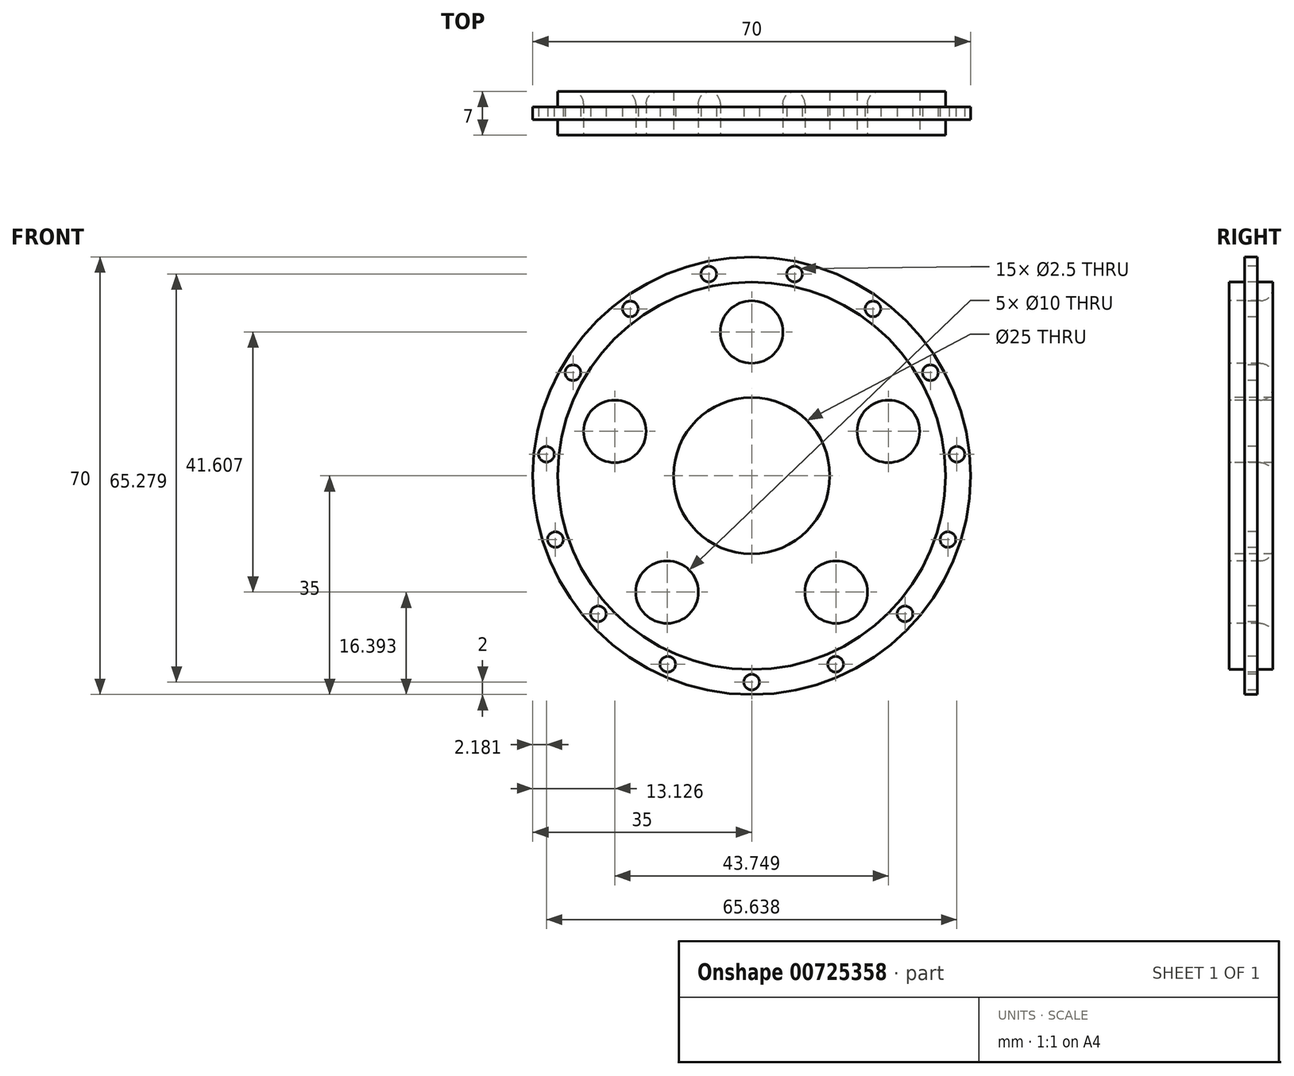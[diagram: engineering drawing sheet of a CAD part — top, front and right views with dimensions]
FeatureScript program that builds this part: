
annotation { "Feature Type Name" : "Feature", "Feature Type Description" : "" }
export const myFeature = defineFeature(function(context is Context, id is Id, definition is map)
    precondition{}
    {
        {
            var Q0;
            Q0=qCreatedBy(makeId("Front.planeOp"),FACE);
            var sketch = newSketch(context, id + "F0", { "sketchPlane" : qUnion([Q0])});
            skCircle(sketch, "E0", {"center": v(0, 0) * mm, "radius": 35 * mm});
            skSolve(sketch);
        }
        {
            var Q0;
            Q0=qSketchRegion(id+"F0",true);
            extrude(context, id + "F1", {"entities" : qUnion([Q0]), "oppositeDirection" : true, "depth" : 3 * mm, "hasSecondDirection" : true, "secondDirectionOppositeDirection" : false, "secondDirectionDepth" : 4 * mm, "offsetDistance" : 25 * mm});
        }
        {
            var Q0;
            Q0=makeQuery(id+"F1.opExtrude","CAP_FACE",FACE,{"disambiguationData":[OSD([sQuery(id+"F0.wireOp",EDGE,"E0")])],"isStart":true});
            var sketch = newSketch(context, id + "F2", { "sketchPlane" : qUnion([Q0])});
            skCircle(sketch, "E1", {"center": v(0, 0) * mm, "radius": 12.5 * mm});
            skSolve(sketch);
        }
        {
            var Q0;
            Q0=qSketchRegion(id+"F2",true);
            extrude(context, id + "F3", {"entities" : qUnion([Q0]), "operationType" : NewBodyOperationType.REMOVE, "oppositeDirection" : true, "depth" : 25 * mm});
        }
        {
            var Q0;
            Q0=makeQuery(id+"F1.opExtrude","CAP_FACE",FACE,{"disambiguationData":[OSD([sQuery(id+"F0.wireOp",EDGE,"E0")])],"isStart":true});
            var sketch = newSketch(context, id + "F4", { "sketchPlane" : qUnion([Q0])});
            skCircle(sketch, "E2", {"center": v(0, 23) * mm, "radius": 5 * mm});
            skLineSegment(sketch, "E3", {"start": v(0, 31) * mm, "end": v(0, 15) * mm, "construction": true});
            skCircle(sketch, "E4.1.0", {"center": v(-21.87, 7.1) * mm, "radius": 5 * mm});
            skCircle(sketch, "E4.2.0", {"center": v(-13.52, -18.6) * mm, "radius": 5 * mm});
            skPoint(sketch, "E4.center", {"position": v(0, 0) * mm});
            skCircle(sketch, "E5", {"center": v(0, 0) * mm, "radius": 15 * mm, "construction": true});
            skCircle(sketch, "E6", {"center": v(0, 0) * mm, "radius": 31 * mm, "construction": true});
            skCircle(sketch, "E7.1.3.0", {"center": v(13.52, -18.6) * mm, "radius": 5 * mm});
            skCircle(sketch, "E8.1.4.0", {"center": v(21.87, 7.1) * mm, "radius": 5 * mm});
            skSolve(sketch);
        }
        {
            var Q0;
            Q0=qSketchRegion(id+"F4",true);
            extrude(context, id + "F5", {"entities" : qUnion([Q0]), "operationType" : NewBodyOperationType.REMOVE, "oppositeDirection" : true, "depth" : 25 * mm});
        }
        {
            var Q0;
            Q0=makeQuery(id+"F1.opExtrude","CAP_FACE",FACE,{"disambiguationData":[OSD([sQuery(id+"F0.wireOp",EDGE,"E0")])],"isStart":true});
            var sketch = newSketch(context, id + "F6", { "sketchPlane" : qUnion([Q0])});
            skCircle(sketch, "E9", {"center": v(0, 0) * mm, "radius": 15 * mm, "construction": true});
            skSolve(sketch);
        }
        {
            var Q0;
            Q0=makeQuery(id+"F5.boolean.opBoolean","COPY",EDGE,{"derivedFrom":makeQuery(id+"F5.opExtrude","CAP_EDGE",EDGE,{"disambiguationData":[OSD([sQuery(id+"F4.wireOp",EDGE,"E2")])],"isStart":true})});
            var Q1;
            Q1=makeQuery(id+"F5.boolean.opBoolean","COPY",EDGE,{"derivedFrom":makeQuery(id+"F5.opExtrude","CAP_EDGE",EDGE,{"disambiguationData":[OSD([sQuery(id+"F4.wireOp",EDGE,"E4.1.0")])],"isStart":true})});
            var Q2;
            Q2=makeQuery(id+"F5.boolean.opBoolean","COPY",EDGE,{"derivedFrom":makeQuery(id+"F5.opExtrude","CAP_EDGE",EDGE,{"disambiguationData":[OSD([sQuery(id+"F4.wireOp",EDGE,"E4.2.0")])],"isStart":true})});
            var Q3;
            Q3=makeQuery(id+"F5.boolean.opBoolean","INTERSECT",EDGE,{"derivedFrom":[makeQuery(id+"F1.opExtrude","CAP_FACE",FACE,{"disambiguationData":[OSD([sQuery(id+"F0.wireOp",EDGE,"E0")])],"isStart":false}),makeQuery(id+"F5.opExtrude","SWEPT_FACE",FACE,{"disambiguationData":[OSD([sQuery(id+"F4.wireOp",EDGE,"E4.1.0")])]})]});
            var Q4;
            Q4=makeQuery(id+"F5.boolean.opBoolean","INTERSECT",EDGE,{"derivedFrom":[makeQuery(id+"F1.opExtrude","CAP_FACE",FACE,{"disambiguationData":[OSD([sQuery(id+"F0.wireOp",EDGE,"E0")])],"isStart":false}),makeQuery(id+"F5.opExtrude","SWEPT_FACE",FACE,{"disambiguationData":[OSD([sQuery(id+"F4.wireOp",EDGE,"E4.2.0")])]})]});
            var Q5;
            Q5=makeQuery(id+"F5.boolean.opBoolean","INTERSECT",EDGE,{"derivedFrom":[makeQuery(id+"F1.opExtrude","CAP_FACE",FACE,{"disambiguationData":[OSD([sQuery(id+"F0.wireOp",EDGE,"E0")])],"isStart":false}),makeQuery(id+"F5.opExtrude","SWEPT_FACE",FACE,{"disambiguationData":[OSD([sQuery(id+"F4.wireOp",EDGE,"E2")])]})]});
            var Q6;
            Q6=makeQuery(id+"F5.boolean.opBoolean","COPY",EDGE,{"derivedFrom":makeQuery(id+"F5.opExtrude","CAP_EDGE",EDGE,{"disambiguationData":[OSD([sQuery(id+"F4.wireOp",EDGE,"a81bae41-d5ea-4544-bfaf-6c99a52da0b9.1.5.0")])],"isStart":true})});
            var Q7;
            Q7=makeQuery(id+"F5.boolean.opBoolean","COPY",EDGE,{"derivedFrom":makeQuery(id+"F5.opExtrude","CAP_EDGE",EDGE,{"disambiguationData":[OSD([sQuery(id+"F4.wireOp",EDGE,"E7.1.4.0")])],"isStart":true})});
            var Q8;
            Q8=makeQuery(id+"F5.boolean.opBoolean","COPY",EDGE,{"derivedFrom":makeQuery(id+"F5.opExtrude","CAP_EDGE",EDGE,{"disambiguationData":[OSD([sQuery(id+"F4.wireOp",EDGE,"E7.1.3.0")])],"isStart":true})});
            var Q9;
            Q9=makeQuery(id+"F5.boolean.opBoolean","INTERSECT",EDGE,{"derivedFrom":[makeQuery(id+"F1.opExtrude","CAP_FACE",FACE,{"disambiguationData":[OSD([sQuery(id+"F0.wireOp",EDGE,"E0")])],"isStart":false}),makeQuery(id+"F5.opExtrude","SWEPT_FACE",FACE,{"disambiguationData":[OSD([sQuery(id+"F4.wireOp",EDGE,"E7.1.3.0")])]})]});
            var Q10;
            Q10=makeQuery(id+"F5.boolean.opBoolean","INTERSECT",EDGE,{"derivedFrom":[makeQuery(id+"F1.opExtrude","CAP_FACE",FACE,{"disambiguationData":[OSD([sQuery(id+"F0.wireOp",EDGE,"E0")])],"isStart":false}),makeQuery(id+"F5.opExtrude","SWEPT_FACE",FACE,{"disambiguationData":[OSD([sQuery(id+"F4.wireOp",EDGE,"E7.1.4.0")])]})]});
            var Q11;
            Q11=makeQuery(id+"F5.boolean.opBoolean","INTERSECT",EDGE,{"derivedFrom":[makeQuery(id+"F1.opExtrude","CAP_FACE",FACE,{"disambiguationData":[OSD([sQuery(id+"F0.wireOp",EDGE,"E0")])],"isStart":false}),makeQuery(id+"F5.opExtrude","SWEPT_FACE",FACE,{"disambiguationData":[OSD([sQuery(id+"F4.wireOp",EDGE,"a81bae41-d5ea-4544-bfaf-6c99a52da0b9.1.5.0")])]})]});
            var Q12;
            Q12=makeQuery(id+"F5.boolean.opBoolean","COPY",EDGE,{"derivedFrom":makeQuery(id+"F5.opExtrude","CAP_EDGE",EDGE,{"disambiguationData":[OSD([sQuery(id+"F4.wireOp",EDGE,"E8.1.4.0")])],"isStart":true})});
            fillet(context, id + "F7", {"entities" : qUnion([Q0, Q1, Q2, Q3, Q4, Q5, Q6, Q7, Q8, Q9, Q10, Q11, Q12]), "radius" : 2 * mm, "tangentPropagation" : true, "allowEdgeOverflow" : false});
        }
        {
            var Q0;
            Q0=makeQuery(id+"F6.imprint","IMPRINT",FACE,{"disambiguationData":[TD([[makeQuery(id+"F6.imprint","IMPRINT",EDGE,{"derivedFrom":makeQuery(id+"F1.opExtrude","CAP_EDGE",EDGE,{"disambiguationData":[OSD([sQuery(id+"F0.wireOp",EDGE,"E0")])],"isStart":true})}),1.0]])]});
            var sketch = newSketch(context, id + "F8", { "sketchPlane" : qUnion([Q0])});
            skCircle(sketch, "E10", {"center": v(0, 0) * mm, "radius": 31 * mm});
            skCircle(sketch, "E11", {"center": v(0, 0) * mm, "radius": 35.22 * mm});
            skSolve(sketch);
        }
        {
            var Q0;
            Q0 = qSketchRegion(id + "F8", true);
            extrude(context, id + "F9", {"entities" : qUnion([Q0]), "operationType" : NewBodyOperationType.REMOVE, "oppositeDirection" : true, "depth" : 2.5 * mm, "offsetDistance" : 25 * mm});
        }
        {
            var Q0;
            Q0=makeQuery(id+"F1.opExtrude","CAP_FACE",FACE,{"disambiguationData":[OSD([sQuery(id+"F0.wireOp",EDGE,"E0")])],"isStart":false});
            var sketch = newSketch(context, id + "F10", { "sketchPlane" : qUnion([Q0])});
            skCircle(sketch, "E12", {"center": v(0, 0) * mm, "radius": 31 * mm});
            skCircle(sketch, "E13", {"center": v(0, 0) * mm, "radius": 40.9 * mm});
            skSolve(sketch);
        }
        {
            var Q0;
            Q0 = qSketchRegion(id + "F10", true);
            extrude(context, id + "F11", {"entities" : qUnion([Q0]), "operationType" : NewBodyOperationType.REMOVE, "oppositeDirection" : true, "depth" : 2.5 * mm, "offsetDistance" : 25 * mm});
        }
        {
            var Q0;
            Q0=makeQuery(id+"F9.boolean.opBoolean","COPY",FACE,{"derivedFrom":makeQuery(id+"F9.opExtrude","CAP_FACE",FACE,{"disambiguationData":[OSD([sQuery(id+"F8.wireOp",EDGE,"E10"),sQuery(id+"F8.wireOp",EDGE,"E11")])],"isStart":false})});
            var sketch = newSketch(context, id + "F12", { "sketchPlane" : qUnion([Q0])});
            skLineSegment(sketch, "E14", {"start": v(0, 33) * mm, "end": v(0, 0) * mm, "construction": true});
            skPoint(sketch, "E15.center", {"position": v(0, 0) * mm});
            skLineSegment(sketch, "E16", {"start": v(0, 0) * mm, "end": v(6.86, 32.28) * mm, "construction": true});
            skCircle(sketch, "E17", {"center": v(6.86, 32.28) * mm, "radius": 1.25 * mm});
            skCircle(sketch, "E18.1.0", {"center": v(-6.86, 32.28) * mm, "radius": 1.25 * mm});
            skLineSegment(sketch, "E18.1.1", {"start": v(0, 0) * mm, "end": v(-6.86, 32.28) * mm, "construction": true});
            skCircle(sketch, "E18.2.0", {"center": v(-19.4, 26.7) * mm, "radius": 1.25 * mm});
            skLineSegment(sketch, "E18.2.1", {"start": v(0, 0) * mm, "end": v(-19.4, 26.7) * mm, "construction": true});
            skCircle(sketch, "E18.3.0", {"center": v(-28.58, 16.5) * mm, "radius": 1.25 * mm});
            skLineSegment(sketch, "E18.3.1", {"start": v(0, 0) * mm, "end": v(-28.58, 16.5) * mm, "construction": true});
            skCircle(sketch, "E18.4.0", {"center": v(-32.82, 3.45) * mm, "radius": 1.25 * mm});
            skLineSegment(sketch, "E18.4.1", {"start": v(0, 0) * mm, "end": v(-32.82, 3.45) * mm, "construction": true});
            skCircle(sketch, "E18.5.0", {"center": v(-31.38, -10.2) * mm, "radius": 1.25 * mm});
            skLineSegment(sketch, "E18.5.1", {"start": v(0, 0) * mm, "end": v(-31.38, -10.2) * mm, "construction": true});
            skCircle(sketch, "E18.6.0", {"center": v(-24.52, -22.08) * mm, "radius": 1.25 * mm});
            skLineSegment(sketch, "E18.6.1", {"start": v(0, 0) * mm, "end": v(-24.52, -22.08) * mm, "construction": true});
            skCircle(sketch, "E18.7.0", {"center": v(-13.42, -30.15) * mm, "radius": 1.25 * mm});
            skLineSegment(sketch, "E18.7.1", {"start": v(0, 0) * mm, "end": v(-13.42, -30.15) * mm, "construction": true});
            skCircle(sketch, "E18.8.0", {"center": v(0, -33) * mm, "radius": 1.25 * mm});
            skLineSegment(sketch, "E18.8.1", {"start": v(0, 0) * mm, "end": v(0, -33) * mm, "construction": true});
            skCircle(sketch, "E18.9.0", {"center": v(13.42, -30.15) * mm, "radius": 1.25 * mm});
            skLineSegment(sketch, "E18.9.1", {"start": v(0, 0) * mm, "end": v(13.42, -30.15) * mm, "construction": true});
            skCircle(sketch, "E19.1.10.0", {"center": v(24.52, -22.08) * mm, "radius": 1.25 * mm});
            skLineSegment(sketch, "E19.2.10.0", {"start": v(0, 0) * mm, "end": v(24.52, -22.08) * mm, "construction": true});
            skCircle(sketch, "E19.1.11.0", {"center": v(31.38, -10.2) * mm, "radius": 1.25 * mm});
            skLineSegment(sketch, "E19.2.11.0", {"start": v(0, 0) * mm, "end": v(31.38, -10.2) * mm, "construction": true});
            skCircle(sketch, "E20.1.12.0", {"center": v(32.82, 3.45) * mm, "radius": 1.25 * mm});
            skLineSegment(sketch, "E20.2.12.0", {"start": v(0, 0) * mm, "end": v(32.82, 3.45) * mm, "construction": true});
            skCircle(sketch, "E20.1.13.0", {"center": v(28.58, 16.5) * mm, "radius": 1.25 * mm});
            skLineSegment(sketch, "E20.2.13.0", {"start": v(0, 0) * mm, "end": v(28.58, 16.5) * mm, "construction": true});
            skCircle(sketch, "E20.1.14.0", {"center": v(19.4, 26.7) * mm, "radius": 1.25 * mm});
            skLineSegment(sketch, "E20.2.14.0", {"start": v(0, 0) * mm, "end": v(19.4, 26.7) * mm, "construction": true});
            skSolve(sketch);
        }
        {
            var Q0;
            Q0 = qSketchRegion(id + "F12", true);
            extrude(context, id + "F13", {"entities" : qUnion([Q0]), "operationType" : NewBodyOperationType.REMOVE, "oppositeDirection" : true, "depth" : 25 * mm, "offsetDistance" : 25 * mm});
        }
    });
